# Revit family: Soap Dispenser_Metlam_Rectangular_Horizontal_Pump
name_source: partatom
category: Specialty Equipment
revit_build: Autodesk Revit 2016 (Build: 20170117_1200(x64)
units: mm (PartAtom-declared; Revit-internal decimal feet)

## family parameters
Always vertical = Yes
Cut with Voids When Loaded = No
OmniClass Number = 23.40.20.21.34
OmniClass Title = Soap Holders, Dispensers
Part Type = Normal
Room Calculation Point = Yes
Round Connector Dimension = Use Diameter
Shared = No
Work Plane-Based = No

## types (1)
- 209w x 123d x 123h (ML 600 AS)
    Description = Horizontal Soap Dispenser - SS
    Indicator_Material = z_Metlam_Plastic_Clear Gray
    Manufacturer = Metlam
    Manufacturer_Overall Depth = 123 mm  [stored 0.403543 ft]
    Manufacturer_Overall Height = 123 mm  [stored 0.403543 ft]
    Manufacturer_Overall Width = 209 mm  [stored 0.685696 ft]
    Manufacturer_Spec Code = ML 600 AS
    Manufacturer_URL__Product Specific = https://metlam.com.au
    Material_ANZRS = z_Metlam_Metal_Stainless Steel_Satin
    Model = ML 600 AS
    Type Comments = Soap Dispensers
    URL = http://www.metlam.com.au

note: [stored X ft] marks values corroborated as IEEE doubles in the binary element streams (Revit-internal decimal feet)

## geometry (parser evidence)
native form markers: Sweep x2
no freeform markers — native parametric forms only
